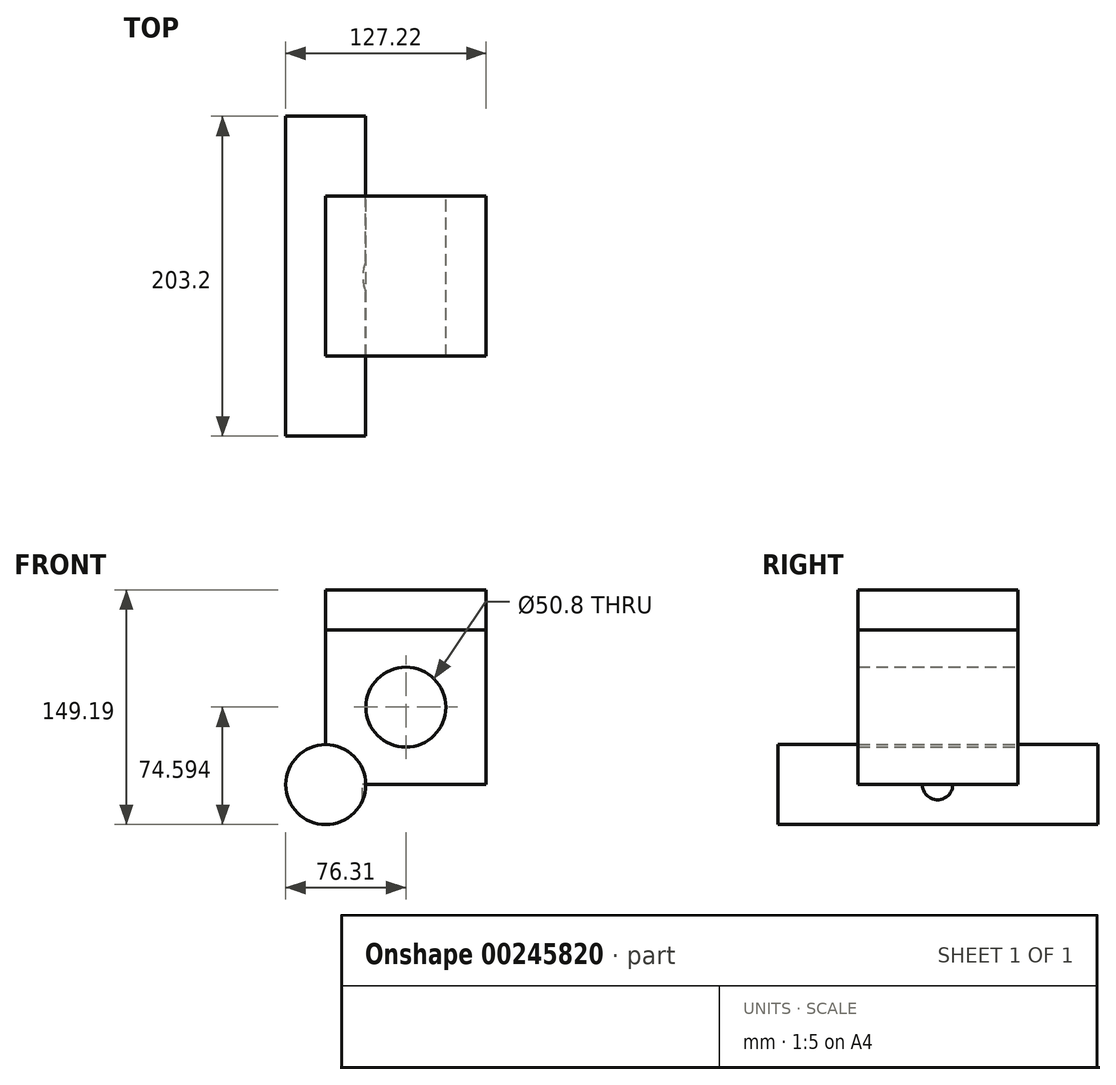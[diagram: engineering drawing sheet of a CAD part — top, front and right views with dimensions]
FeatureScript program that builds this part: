
annotation { "Feature Type Name" : "Feature", "Feature Type Description" : "" }
export const myFeature = defineFeature(function(context is Context, id is Id, definition is map)
    precondition{}
    {
        {
            var Q0;
            Q0=qCreatedBy(makeId("Front.planeOp"),FACE);
            var sketch = newSketch(context, id + "F0", { "sketchPlane" : qUnion([Q0])});
            skLineSegment(sketch, "E0", {"start": v(0, 0) * mm, "end": v(101.82, 0) * mm});
            skLineSegment(sketch, "E1", {"start": v(101.82, 0) * mm, "end": v(101.82, 98.39) * mm});
            skLineSegment(sketch, "E2", {"start": v(0, 98.39) * mm, "end": v(0, 0) * mm});
            skLineSegment(sketch, "E3", {"start": v(0, 98.39) * mm, "end": v(101.82, 98.39) * mm});
            skCircle(sketch, "E4", {"center": v(50.91, 49.2) * mm, "radius": 25.4 * mm});
            skPoint(sketch, "E5.orphan", {"position": v(50.91, 98.39) * mm});
            skPoint(sketch, "E6.end.orphan", {"position": v(50.91, 0) * mm});
            skSolve(sketch);
        }
        {
            var Q0;
            Q0 = qSketchRegion(id + "F0", true);
            extrude(context, id + "F1", {"entities" : qUnion([Q0]), "depth" : 101.6 * mm});
        }
        {
            var Q0;
            Q0=qCreatedBy(makeId("Top.planeOp"),FACE);
            var sketch = newSketch(context, id + "F2", { "sketchPlane" : qUnion([Q0])});
            skCircle(sketch, "E7", {"center": v(48.92, -51.1) * mm, "radius": 25.4 * mm});
            skPoint(sketch, "E8.orphan", {"position": v(48.92, 0) * mm});
            skPoint(sketch, "E9.end.orphan", {"position": v(48.92, -102.2) * mm});
            skSolve(sketch);
        }
        {
            var Q0;
            Q0=qCreatedBy(makeId("Front.planeOp"),FACE);
            cPlane(context, id + "F3", {"entities" : qUnion([Q0]), "cplaneType" : CPlaneType.OFFSET, "offset" : 101.6 * mm, "width" : 152.4 * mm, "height" : 152.4 * mm});
        }
        {
            var Q0;
            Q0=qCreatedBy(id+"F3.planeOp",FACE);
            var sketch = newSketch(context, id + "F4", { "sketchPlane" : qUnion([Q0])});
            skCircle(sketch, "E10", {"center": v(0, 0) * mm, "radius": 25.4 * mm});
            skSolve(sketch);
        }
        {
            var Q0;
            Q0 = qSketchRegion(id + "F4", true);
            extrude(context, id + "F5", {"entities" : qUnion([Q0]), "operationType" : NewBodyOperationType.ADD, "depth" : 50.8 * mm, "hasSecondDirection" : true, "secondDirectionOppositeDirection" : true, "secondDirectionDepth" : 152.4 * mm});
        }
        {
            var Q0;
            Q0=makeQuery(id+"F1.opExtrude","SWEPT_FACE",FACE,{"disambiguationData":[OSD([sQuery(id+"F0.wireOp",EDGE,"E3")])]});
            extrude(context, id + "F6", {"entities" : qUnion([Q0]), "depth" : 25.4 * mm});
        }
        {
            var Q0;
            Q0=makeQuery(id+"F2.imprint","IMPRINT",FACE,{"disambiguationData":[TD([[makeQuery(id+"F2.imprint","IMPRINT",EDGE,{"derivedFrom":sQuery(id+"F2.wireOp",EDGE,"E7")}),1.0]])]});
            extrude(context, id + "F7", {"entities" : qUnion([Q0]), "operationType" : NewBodyOperationType.REMOVE, "oppositeDirection" : true, "depth" : 25.4 * mm});
        }
    });
